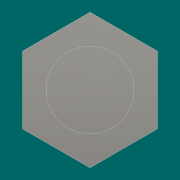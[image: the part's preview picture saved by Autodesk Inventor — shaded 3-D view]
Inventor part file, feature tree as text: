
AUTODESK INVENTOR PART (.ipt)
format: ipt  version: 2019 (Build 230136000, 136)  size: 113,664 bytes
history: native  units: mm
features: extrude x3, sketch x3, thread x2
ambient origin geometry x8: Origin, YZ Plane, XZ Plane, XY Plane, X Axis, Y Axis, Z Axis, Center Point
bodies: Body1 (feature_tree)
feature tree (8):
  extrude  "Extrusion3"  Depth=15.0mm TaperAngle=0.0deg
  extrude  "Extrusion4"  Depth=6.0mm TaperAngle=0.0deg
  thread  "Thread2"  [1 undecoded]
  extrude  "Extrusion5"  Depth=6.0mm TaperAngle=0.0deg
  thread  "Thread3"  [1 undecoded]
  sketch  "Sketch6"  dims[d15=4.6mm d16=15.0mm d17=0.0mm]
  sketch  "Sketch7"  dims[d18=3.0mm d19=6.0mm d20=0.0mm d21=10.0mm d22=0.0mm]
  sketch  "Sketch8"  dims[d23=3.0mm d24=6.0mm d25=0.0mm d26=10.0mm d27=0.0mm]
note: 2 required parameter values undecoded (feature->parameter linkage not recoverable at this tier; creation-order binding heuristic only, values carry confidence <= 0.55)
